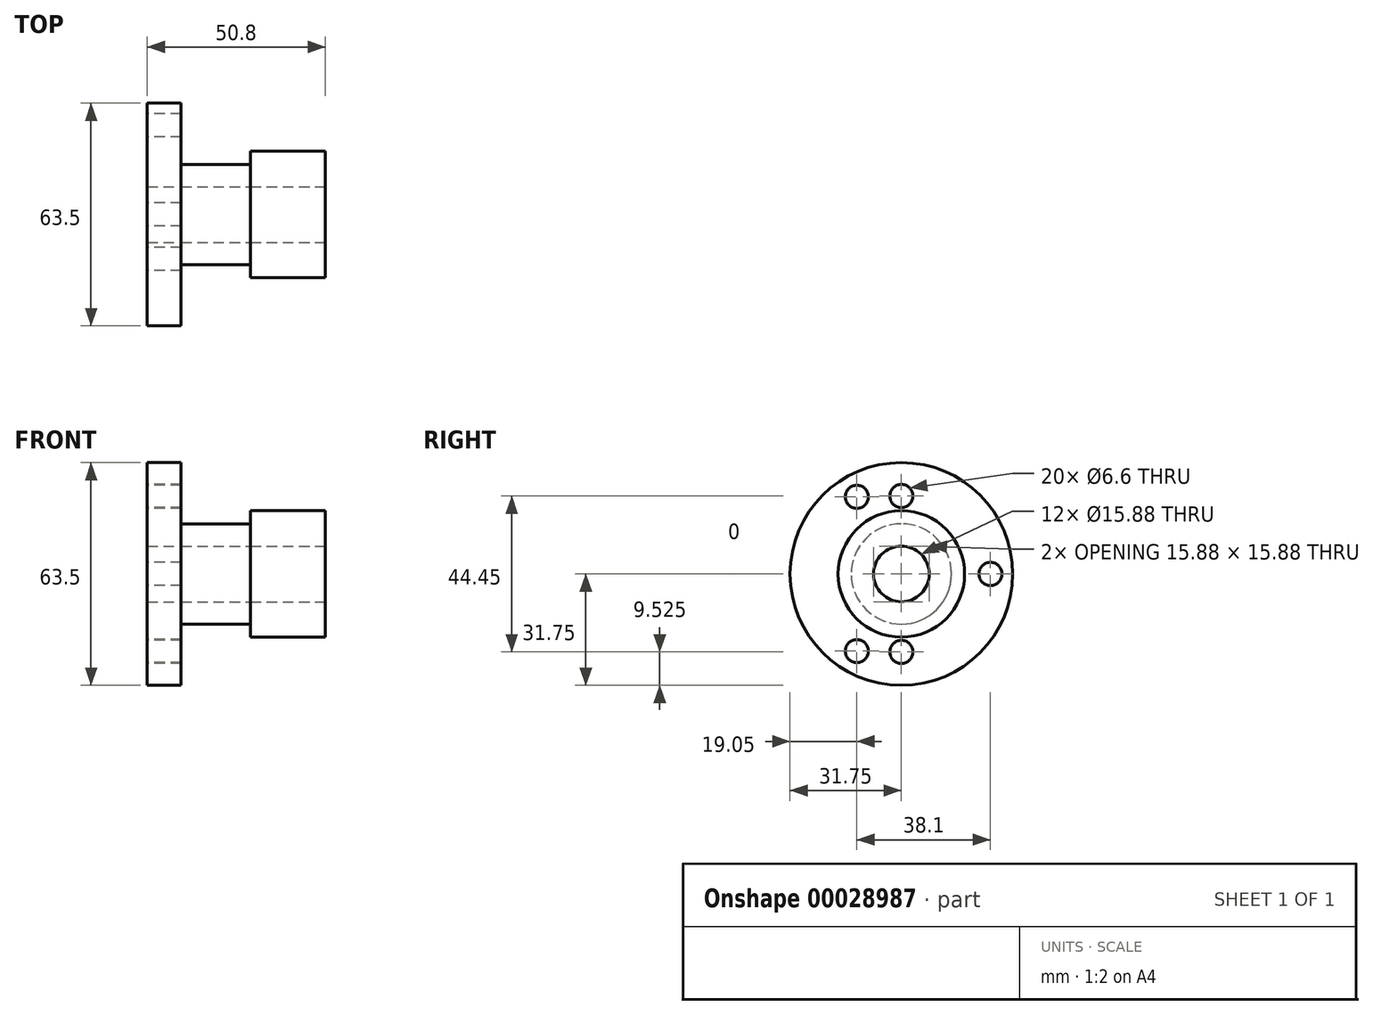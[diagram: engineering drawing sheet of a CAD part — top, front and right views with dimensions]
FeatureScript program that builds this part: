
annotation { "Feature Type Name" : "Feature", "Feature Type Description" : "" }
export const myFeature = defineFeature(function(context is Context, id is Id, definition is map)
    precondition{}
    {
        {
            var Q0;
            Q0=qCreatedBy(makeId("Right.planeOp"),FACE);
            var sketch = newSketch(context, id + "F0", { "sketchPlane" : qUnion([Q0])});
            skCircle(sketch, "E0", {"center": v(0, 0) * mm, "radius": 31.75 * mm});
            skCircle(sketch, "E1", {"center": v(0, 0) * mm, "radius": 25.4 * mm, "construction": true});
            skLineSegment(sketch, "E2", {"start": v(0, 0) * mm, "end": v(0, 43.65) * mm, "construction": true});
            skLineSegment(sketch, "E3", {"start": v(0, 0) * mm, "end": v(-22.57, 39.1) * mm, "construction": true});
            skCircle(sketch, "E4", {"center": v(-12.7, 22) * mm, "radius": 3.3 * mm});
            skCircle(sketch, "E5.1.0", {"center": v(-12.7, -22) * mm, "radius": 3.3 * mm});
            skCircle(sketch, "E5.2.0", {"center": v(25.4, 0) * mm, "radius": 3.3 * mm});
            skCircle(sketch, "E6", {"center": v(0, 0) * mm, "radius": 22.23 * mm, "construction": true});
            skCircle(sketch, "E7", {"center": v(0, 22.23) * mm, "radius": 3.3 * mm});
            skCircle(sketch, "E8.1.0", {"center": v(0, -22.23) * mm, "radius": 3.3 * mm});
            skSolve(sketch);
        }
        {
            var Q0;
            Q0 = qSketchRegion(id + "F0", true);
            extrude(context, id + "F1", {"entities" : qUnion([Q0]), "depth" : 9.65 * mm});
        }
        {
            var Q0;
            Q0=qCreatedBy(makeId("Right.planeOp"),FACE);
            cPlane(context, id + "F2", {"entities" : qUnion([Q0]), "cplaneType" : CPlaneType.OFFSET, "offset" : 50.8 * mm, "width" : 152.4 * mm, "height" : 152.4 * mm});
        }
        {
            var Q0;
            Q0=qCreatedBy(id+"F2.planeOp",FACE);
            var sketch = newSketch(context, id + "F3", { "sketchPlane" : qUnion([Q0])});
            skCircle(sketch, "E9", {"center": v(0, 0) * mm, "radius": 18.03 * mm});
            skSolve(sketch);
        }
        {
            var Q0;
            Q0 = qSketchRegion(id + "F3", true);
            extrude(context, id + "F4", {"entities" : qUnion([Q0]), "oppositeDirection" : true, "depth" : 21.34 * mm});
        }
        {
            var Q0;
            Q0=makeQuery(id+"F4.opExtrude","CAP_FACE",FACE,{"disambiguationData":[OSD([sQuery(id+"F3.wireOp",EDGE,"E9")])],"isStart":false});
            var sketch = newSketch(context, id + "F5", { "sketchPlane" : qUnion([Q0])});
            skCircle(sketch, "E10", {"center": v(0, 0) * mm, "radius": 14.3 * mm});
            skSolve(sketch);
        }
        {
            var Q0;
            Q0 = qSketchRegion(id + "F5", true);
            var Q1;
            Q1=makeQuery(id+"F1.opExtrude","CAP_FACE",FACE,{"disambiguationData":[OSD([sQuery(id+"F0.wireOp",EDGE,"E0"),sQuery(id+"F0.wireOp",EDGE,"E4"),sQuery(id+"F0.wireOp",EDGE,"E5.1.0"),sQuery(id+"F0.wireOp",EDGE,"E5.2.0"),sQuery(id+"F0.wireOp",EDGE,"E7"),sQuery(id+"F0.wireOp",EDGE,"E8.1.0")])],"isStart":false});
            extrude(context, id + "F6", {"entities" : qUnion([Q0]), "endBound" : BoundingType.UP_TO_SURFACE, "endBoundEntityFace" : qUnion([Q1]), "depth" : 25.4 * mm});
        }
        {
            var Q0;
            Q0=makeQuery(id+"F4.opExtrude","CAP_FACE",FACE,{"disambiguationData":[OSD([sQuery(id+"F3.wireOp",EDGE,"E9")])],"isStart":true});
            var sketch = newSketch(context, id + "F7", { "sketchPlane" : qUnion([Q0])});
            skCircle(sketch, "E11", {"center": v(0, 0) * mm, "radius": 7.94 * mm});
            skSolve(sketch);
        }
        {
            var Q0;
            Q0 = qSketchRegion(id + "F7", true);
            extrude(context, id + "F8", {"entities" : qUnion([Q0]), "operationType" : NewBodyOperationType.REMOVE, "endBound" : BoundingType.THROUGH_ALL, "oppositeDirection" : true, "depth" : 25.4 * mm});
        }
    });
